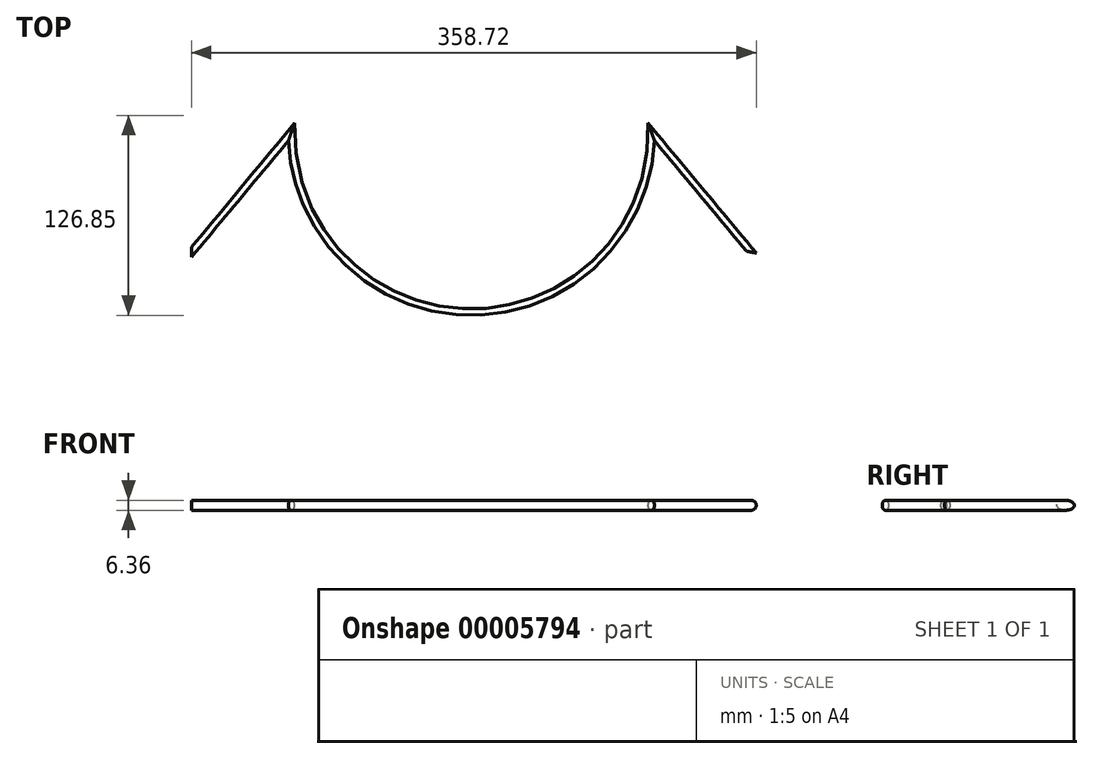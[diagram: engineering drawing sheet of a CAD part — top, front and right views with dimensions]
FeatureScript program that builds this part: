
annotation { "Feature Type Name" : "Feature", "Feature Type Description" : "" }
export const myFeature = defineFeature(function(context is Context, id is Id, definition is map)
    precondition{}
    {
        {
            var Q0;
            Q0=qCreatedBy(makeId("Top.planeOp"),FACE);
            var sketch = newSketch(context, id + "F0", { "sketchPlane" : qUnion([Q0])});
            skLineSegment(sketch, "E0", {"start": v(0, 0) * mm, "end": v(63.5, 76.2) * mm});
            skArc(sketch, "E1", {"start": v(63.5, 76.2) * mm, "mid": v(177.8, -38.1) * mm, "end": v(292.1, 76.2) * mm});
            skLineSegment(sketch, "E2", {"start": v(292.1, 76.2) * mm, "end": v(355.6, 0) * mm});
            skSolve(sketch);
        }
        {
            var Q0;
            Q0=qCreatedBy(makeId("Right.planeOp"),FACE);
            var sketch = newSketch(context, id + "F1", { "sketchPlane" : qUnion([Q0])});
            skCircle(sketch, "E3", {"center": v(0, 0) * mm, "radius": 3.18 * mm});
            skSolve(sketch);
        }
        {
            var Q0;
            Q0 = qSketchRegion(id + "F1", true);
            var Q1;
            Q1 = qBodyType(qCreatedBy(id + "F0" ,EDGE), BodyType.WIRE);
            sweep(context, id + "F2", {"profiles" : qUnion([Q0]), "path" : qUnion([Q1])});
        }
    });
